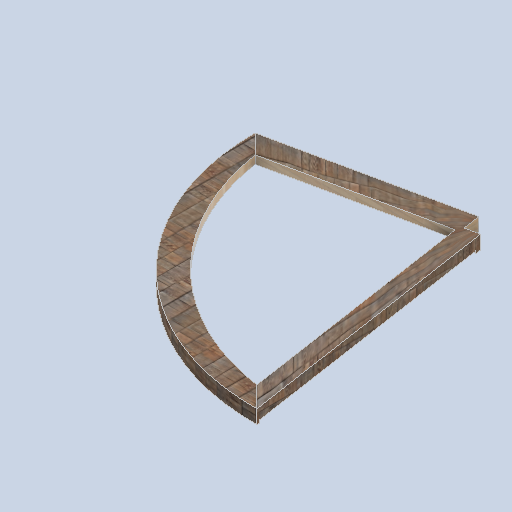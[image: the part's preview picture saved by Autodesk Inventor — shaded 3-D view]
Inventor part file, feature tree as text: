
AUTODESK INVENTOR PART (.ipt)
format: ipt  version: 2024.2 (Build 282272000, 272)  size: 642,560 bytes
history: native  units: in
note: dims shown in document units (in); Inventor stores cm internally (conversion verified against a paired STEP export)
features: sketch x32, extrude x15, projected_geometry x10, plane x7, other x5, loft x1
ambient origin geometry x8: Origin, YZ Plane, XZ Plane, XY Plane, X Axis, Y Axis, Z Axis, Center Point
bodies: Solid1 (feature_tree)
feature tree (70):
  other  "eave_frame_03.ipt"
  extrude  "Extrusion1"  Depth=102.3622in
  sketch  "Sketch16"  dims[d39=102.3622in d40=1.9685in d41=0.0in]
  extrude  "Extrusion2"  TaperAngle=0.0deg  [1 undecoded]
  extrude  "Extrusion3"  Depth=7.0866in TaperAngle=0.0deg
  extrude  "Extrusion4"  Depth=1.9685in TaperAngle=0.0deg
  extrude  "Extrusion5"  TaperAngle=90.0deg  [1 undecoded]
  sketch  "Sketch23"
  extrude  "Extrusion6"  Depth=0.0687in
  extrude  "Extrusion7"  Depth=1.1681in
  extrude  "Extrusion8"  Depth=1.9685in TaperAngle=0.0deg
  sketch  "Sketch26"
  extrude  "Extrusion9"  Depth=102.3622in
  sketch  "Sketch28"
  extrude  "Extrusion10"  Depth=1.9685in TaperAngle=0.0deg
  extrude  "Extrusion11"  Depth=102.3622in
  extrude  "Extrusion12"  Depth=1.9685in TaperAngle=0.0deg
  extrude  "Extrusion13"  TaperAngle=135.0deg  [1 undecoded]
  extrude  "Extrusion14"  TaperAngle=0.0deg  [1 undecoded]
  sketch  "Sketch34"
  sketch  "Sketch36"
  sketch  "Sketch37"
  plane  "Work Plane7"
  loft  "Loft1"
  extrude  "Extrusion15"  Depth=0.0344in
  other  "Solid1::eave_frame_03.ipt"
  other  "TaggingFeature1"
  sketch  "Sketch1"  dims[d0=0.3937in d4=102.3622in]
  sketch  "Sketch2"  dims[d5=1.1811in d6=0.0in d7=0.0in]
  sketch  "Sketch5"  dims[d8=0.0687in d9=7.0866in d10=0.0in]
  sketch  "Sketch6"  dims[d11=7.0866in d12=0.0in d13=1.9685in d14=0.0in]
  sketch  "Sketch7"  dims[d15=1.9685in d16=0.0in d17=90.0deg]
  sketch  "Sketch8"  dims[d18=0.3937in d19=0.0in d20=0.0687in]
  sketch  "Sketch9"  dims[d21=0.0in d22=0.0in d24=1.1681in]
  sketch  "Sketch10"  dims[d25=0.0in d26=0.0in d27=1.9685in d28=0.0in]
  sketch  "Sketch11"  dims[d30=1.9685in d31=0.0in d32=102.3622in]
  sketch  "Sketch12"  dims[d33=102.3622in d34=1.9685in d35=0.0in]
  plane  "Work Plane1"
  plane  "Work Plane2"
  plane  "Work Plane3"
  plane  "Work Plane4"
  plane  "Work Plane5"
  plane  "Work Plane6"
  sketch  "Sketch15"  dims[d36=1.9685in d37=0.0in d38=102.3622in]
  sketch  "Sketch19"  dims[d42=1.9685in d43=0.0in d44=135.0deg]
  projected_geometry  "Projected Loop1"
  sketch  "Sketch20"  dims[d46=0.0in d47=90.0deg d48=0.0in d49=90.0deg]
  sketch  "Sketch21"  dims[d50=0.0in d51=90.0deg d52=1.378in d53=0.0in]
  sketch  "Sketch22"  dims[d29=19.685in d45=0.0344in]
  projected_geometry  "Projected Loop2"
  sketch  "Sketch24"
  sketch  "Sketch25"
  projected_geometry  "Projected Loop3"
  sketch  "Sketch27"
  sketch  "Sketch29"
  sketch  "Sketch30"
  projected_geometry  "Projected Loop4"
  sketch  "Sketch31"
  projected_geometry  "Projected Loop5"
  sketch  "Sketch32"
  sketch  "Sketch33"
  projected_geometry  "Projected Loop6"
  projected_geometry  "Projected Loop7"
  projected_geometry  "Projected Loop8"
  projected_geometry  "Projected Loop9"
  sketch  "Sketch38"
  other  "Edges1"
  other  "Edges2"
  sketch  "Sketch40"
  projected_geometry  "Projected Loop10"
note: 4 required parameter values undecoded (feature->parameter linkage not recoverable at this tier; creation-order binding heuristic only, values carry confidence <= 0.55)
